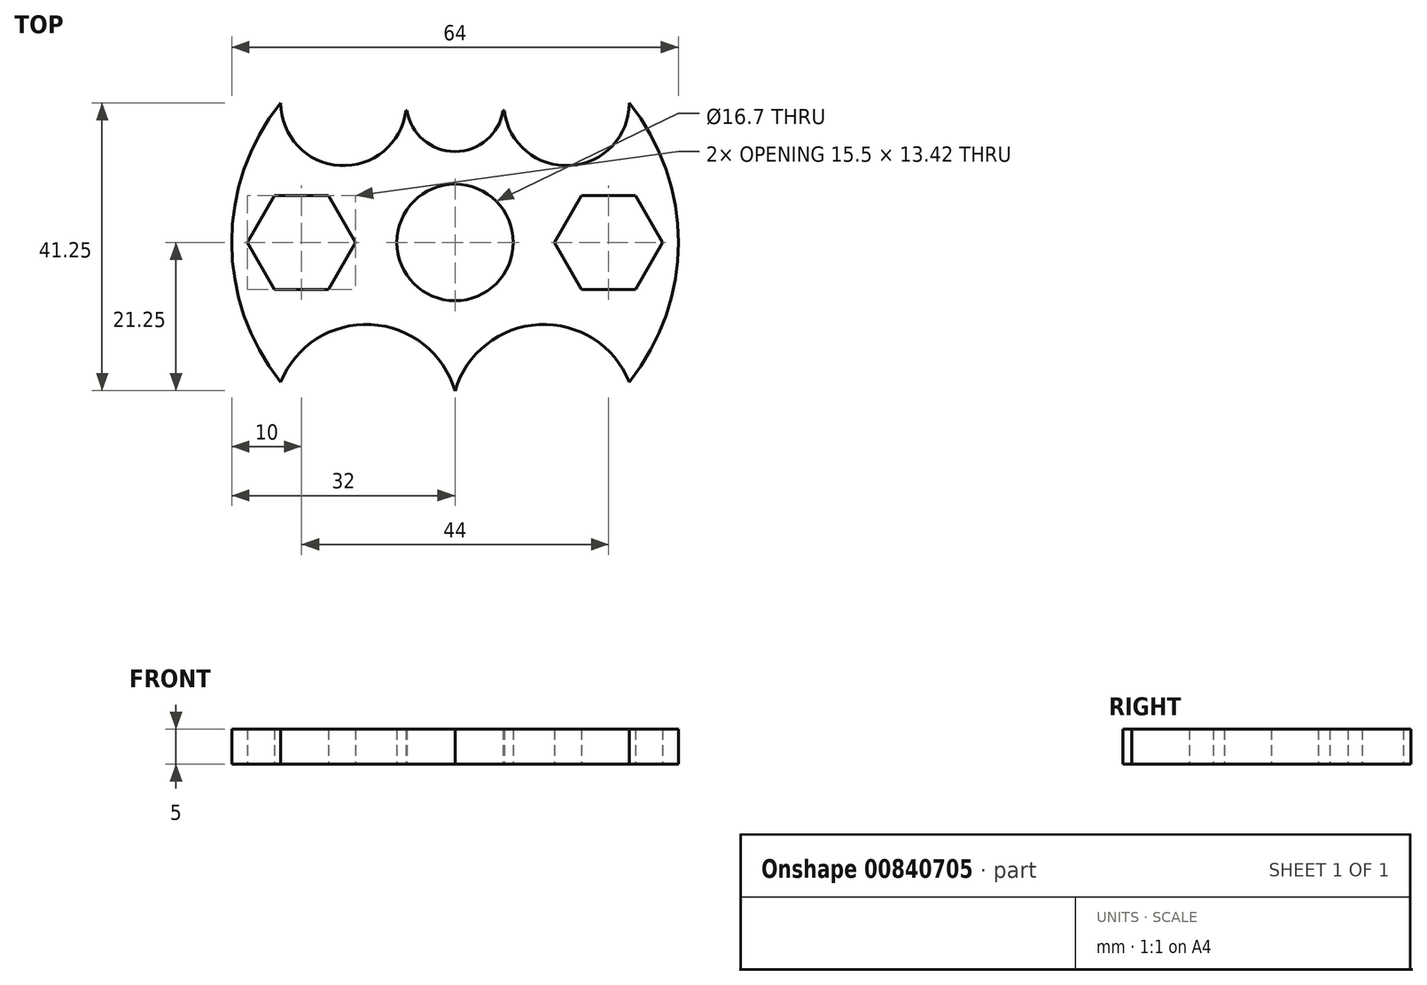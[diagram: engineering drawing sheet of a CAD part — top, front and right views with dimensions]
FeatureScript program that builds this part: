
annotation { "Feature Type Name" : "Feature", "Feature Type Description" : "" }
export const myFeature = defineFeature(function(context is Context, id is Id, definition is map)
    precondition{}
    {
        {
            var Q0;
            Q0=qCreatedBy(makeId("Top.planeOp"),FACE);
            var sketch = newSketch(context, id + "F0", { "sketchPlane" : qUnion([Q0])});
            skCircle(sketch, "E0", {"center": v(0, 0) * mm, "radius": 8.35 * mm});
            skCircle(sketch, "E1", {"center": v(0, 0) * mm, "radius": 32 * mm});
            skLineSegment(sketch, "E2", {"start": v(-24.98, 20) * mm, "end": v(24.98, 20) * mm});
            skLineSegment(sketch, "E3", {"start": v(24.98, 20) * mm, "end": v(24.98, -20) * mm});
            skLineSegment(sketch, "E4", {"start": v(24.98, -20) * mm, "end": v(-24.98, -20) * mm});
            skLineSegment(sketch, "E5", {"start": v(-24.98, -20) * mm, "end": v(-24.98, 20) * mm});
            skCircle(sketch, "E6", {"center": v(-15.98, 20) * mm, "radius": 9 * mm});
            skCircle(sketch, "E7", {"center": v(0, 20) * mm, "radius": 6.98 * mm});
            skCircle(sketch, "E8", {"center": v(15.98, 20) * mm, "radius": 9 * mm});
            skLineSegment(sketch, "E9", {"start": v(-39.73, -25) * mm, "end": v(46.37, -25) * mm, "construction": true});
            skCircle(sketch, "E10", {"center": v(-12.7, -25) * mm, "radius": 13.25 * mm});
            skCircle(sketch, "E11", {"center": v(12.7, -25) * mm, "radius": 13.25 * mm});
            skCircle(sketch, "E12.cCircle", {"center": v(-22, 0) * mm, "radius": 7.75 * mm, "construction": true});
            skLineSegment(sketch, "E12.0", {"start": v(-18.13, -6.71) * mm, "end": v(-25.87, -6.71) * mm});
            skLineSegment(sketch, "E12.1", {"start": v(-25.87, -6.71) * mm, "end": v(-29.75, 0) * mm});
            skLineSegment(sketch, "E12.2", {"start": v(-29.75, 0) * mm, "end": v(-25.87, 6.71) * mm});
            skLineSegment(sketch, "E12.3", {"start": v(-25.87, 6.71) * mm, "end": v(-18.13, 6.71) * mm});
            skLineSegment(sketch, "E12.4", {"start": v(-18.13, 6.71) * mm, "end": v(-14.25, 0) * mm});
            skLineSegment(sketch, "E12.5", {"start": v(-14.25, 0) * mm, "end": v(-18.13, -6.71) * mm});
            skCircle(sketch, "E13.cCircle", {"center": v(22, 0) * mm, "radius": 7.75 * mm, "construction": true});
            skLineSegment(sketch, "E13.0", {"start": v(29.75, 0) * mm, "end": v(25.87, -6.71) * mm});
            skLineSegment(sketch, "E13.1", {"start": v(25.87, -6.71) * mm, "end": v(18.13, -6.71) * mm});
            skLineSegment(sketch, "E13.2", {"start": v(18.13, -6.71) * mm, "end": v(14.25, 0) * mm});
            skLineSegment(sketch, "E13.3", {"start": v(14.25, 0) * mm, "end": v(18.13, 6.71) * mm});
            skLineSegment(sketch, "E13.4", {"start": v(18.13, 6.71) * mm, "end": v(25.87, 6.71) * mm});
            skLineSegment(sketch, "E13.5", {"start": v(25.87, 6.71) * mm, "end": v(29.75, 0) * mm});
            skLineSegment(sketch, "E14", {"start": v(6.9, 18.9) * mm, "end": v(7.05, 18.9) * mm});
            skLineSegment(sketch, "E15", {"start": v(6.9, 18.9) * mm, "end": v(-7.05, 18.9) * mm});
            skSolve(sketch);
        }
        {
            var Q0;
            {var subQ0=sQuery(id+"F0.wireOp",EDGE,"E12.2");var subQ1=sQuery(id+"F0.wireOp",EDGE,"E12.1");var subQ2=makeQuery(id+"F0.imprint","INTERSECT",VERTEX,{"derivedFrom":[subQ1,subQ0]});Q0=makeQuery(id+"F0.imprint","IMPRINT",FACE,{"disambiguationData":[TD([[makeQuery(id+"F0.imprint","IMPRINT",EDGE,{"disambiguationData":[TD([[subQ2,1.0]])],"derivedFrom":subQ1}),1.0]])]});}
            var Q1;
            {var subQ3=sQuery(id+"F0.wireOp",EDGE,"E13.0");var subQ5=sQuery(id+"F0.wireOp",EDGE,"E13.5");var subQ6=makeQuery(id+"F0.imprint","INTERSECT",VERTEX,{"derivedFrom":[subQ3,subQ5]});Q1=makeQuery(id+"F0.imprint","IMPRINT",FACE,{"disambiguationData":[TD([[makeQuery(id+"F0.imprint","IMPRINT",EDGE,{"disambiguationData":[TD([[subQ6,-1.0]])],"derivedFrom":subQ3}),1.0]])]});}
            var Q2;
            Q2=makeQuery(id+"F0.imprint","IMPRINT",FACE,{"disambiguationData":[TD([[makeQuery(id+"F0.imprint","IMPRINT",EDGE,{"derivedFrom":sQuery(id+"F0.wireOp",EDGE,"E0")}),-1.0]])]});
            var Q3;
            {var subQ0=sQuery(id+"F0.wireOp",EDGE,"E11");var subQ1=sQuery(id+"F0.wireOp",EDGE,"E4");var subQ2=makeQuery(id+"F0.imprint","INTERSECT",VERTEX,{"derivedFrom":[subQ1,subQ0]});Q3=makeQuery(id+"F0.imprint","IMPRINT",FACE,{"disambiguationData":[TD([[makeQuery(id+"F0.imprint","IMPRINT",EDGE,{"disambiguationData":[TD([[subQ2,-1.0]])],"derivedFrom":subQ1}),1.0]])]});}
            extrude(context, id + "F1", {"entities" : qUnion([Q0, Q1, Q2, Q3]), "depth" : 5 * mm, "offsetDistance" : 25 * mm});
        }
    });
